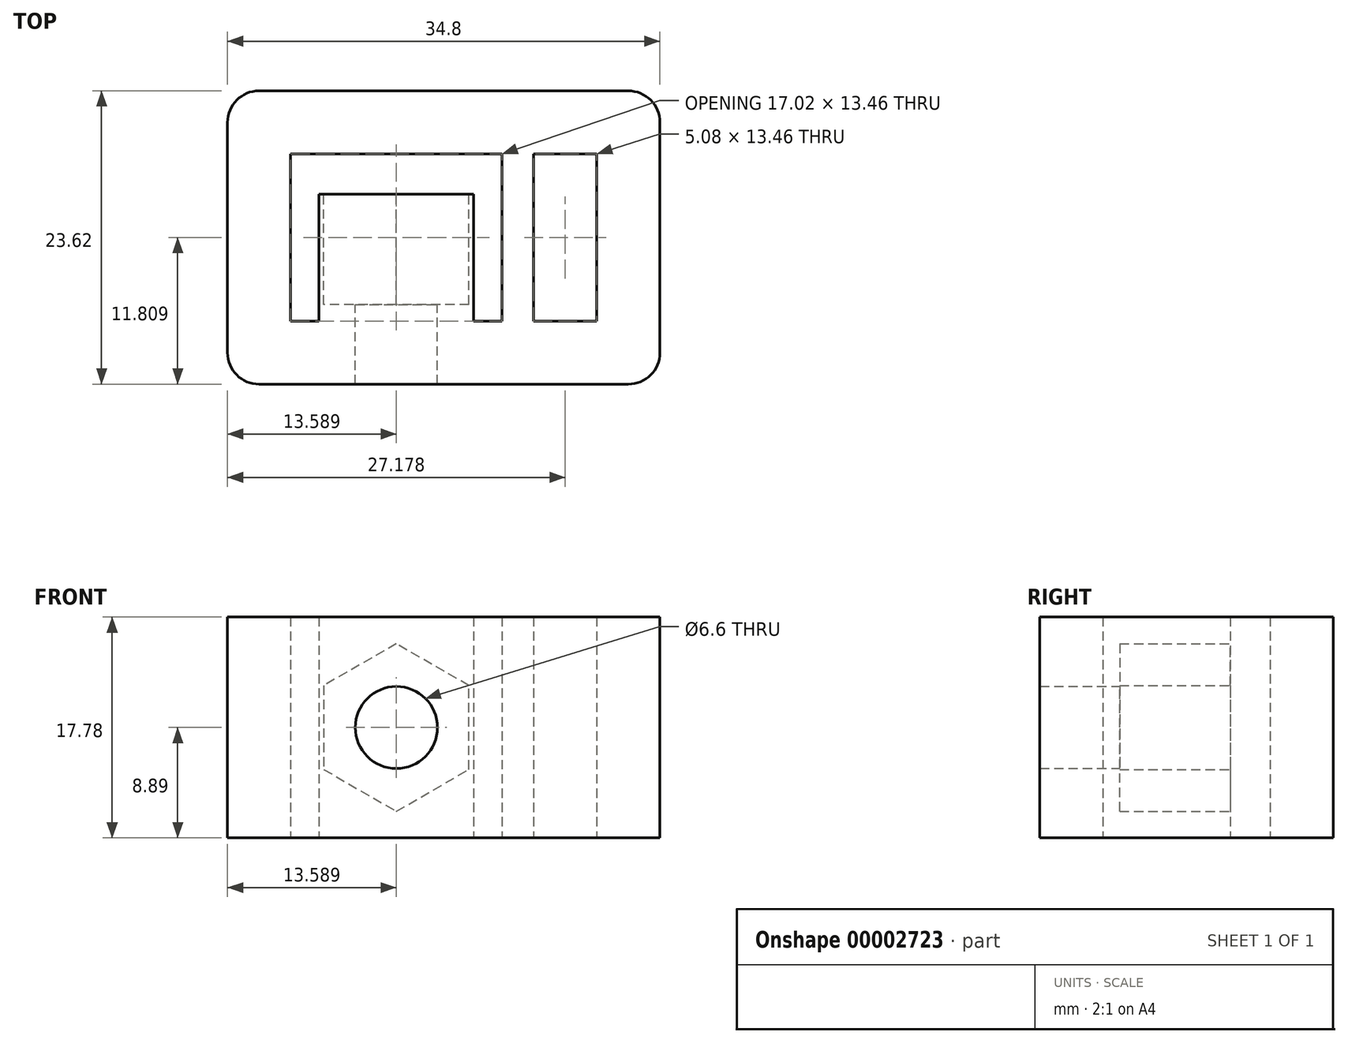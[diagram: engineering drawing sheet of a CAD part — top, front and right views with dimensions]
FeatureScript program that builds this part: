
annotation { "Feature Type Name" : "Feature", "Feature Type Description" : "" }
export const myFeature = defineFeature(function(context is Context, id is Id, definition is map)
    precondition{}
    {
        {
            var Q0;
            Q0=qCreatedBy(makeId("Top.planeOp"),FACE);
            var sketch = newSketch(context, id + "F0", { "sketchPlane" : qUnion([Q0])});
            skLineSegment(sketch, "E0", {"start": v(0, 0) * mm, "end": v(17.02, 0) * mm});
            skLineSegment(sketch, "E1", {"start": v(17.02, 0) * mm, "end": v(17.02, -13.46) * mm});
            skLineSegment(sketch, "E2", {"start": v(17.02, -13.46) * mm, "end": v(14.73, -13.46) * mm});
            skLineSegment(sketch, "E3", {"start": v(14.73, -13.46) * mm, "end": v(14.73, -3.23) * mm});
            skLineSegment(sketch, "E4", {"start": v(14.73, -3.23) * mm, "end": v(2.29, -3.23) * mm});
            skLineSegment(sketch, "E5", {"start": v(2.29, -3.23) * mm, "end": v(2.29, -13.46) * mm});
            skLineSegment(sketch, "E6", {"start": v(2.29, -13.46) * mm, "end": v(0, -13.46) * mm});
            skLineSegment(sketch, "E7", {"start": v(0, -13.46) * mm, "end": v(0, 0) * mm});
            skLineSegment(sketch, "E8", {"start": v(17.02, -13.46) * mm, "end": v(19.56, -13.46) * mm, "construction": true});
            skLineSegment(sketch, "E9", {"start": v(17.02, 0) * mm, "end": v(19.56, 0) * mm, "construction": true});
            skLineSegment(sketch, "E10", {"start": v(19.56, -13.46) * mm, "end": v(19.56, 0) * mm});
            skLineSegment(sketch, "E11", {"start": v(24.64, 0) * mm, "end": v(24.64, -13.46) * mm});
            skLineSegment(sketch, "E12", {"start": v(24.64, -13.46) * mm, "end": v(19.56, -13.46) * mm});
            skLineSegment(sketch, "E13", {"start": v(24.64, 0) * mm, "end": v(19.56, 0) * mm});
            skSolve(sketch);
        }
        {
            var Q0;
            Q0=qCreatedBy(makeId("Top.planeOp"),FACE);
            var sketch = newSketch(context, id + "F1", { "sketchPlane" : qUnion([Q0])});
            skLineSegment(sketch, "E14", {"start": v(0, 0) * mm, "end": v(0, 5.08) * mm, "construction": true});
            skLineSegment(sketch, "E15", {"start": v(0, 5.08) * mm, "end": v(-5.08, 5.08) * mm, "construction": true});
            skLineSegment(sketch, "E16", {"start": v(24.64, -13.46) * mm, "end": v(24.64, -18.54) * mm, "construction": true});
            skLineSegment(sketch, "E17", {"start": v(24.64, -18.54) * mm, "end": v(29.72, -18.54) * mm, "construction": true});
            skSolve(sketch);
        }
        {
            var Q0;
            Q0=qCreatedBy(makeId("Top.planeOp"),FACE);
            var sketch = newSketch(context, id + "F2", { "sketchPlane" : qUnion([Q0])});
            skLineSegment(sketch, "E18.bottom", {"start": v(-5.08, 5.08) * mm, "end": v(29.72, 5.08) * mm});
            skLineSegment(sketch, "E18.top", {"start": v(-5.08, -18.54) * mm, "end": v(29.72, -18.54) * mm});
            skLineSegment(sketch, "E18.left", {"start": v(-5.08, 5.08) * mm, "end": v(-5.08, -18.54) * mm});
            skLineSegment(sketch, "E18.right", {"start": v(29.72, 5.08) * mm, "end": v(29.72, -18.54) * mm});
            skSolve(sketch);
        }
        {
            var Q0;
            Q0=makeQuery(id+"F2.imprint","IMPRINT",FACE,{"disambiguationData":[TD([[makeQuery(id+"F2.imprint","IMPRINT",EDGE,{"derivedFrom":sQuery(id+"F2.wireOp",EDGE,"E18.bottom")}),-1.0]])]});
            extrude(context, id + "F3", {"entities" : qUnion([Q0]), "depth" : 17.78 * mm});
        }
        {
            var Q0;
            {Q0=qUnion([makeQuery(id+"F0.imprint","IMPRINT",FACE,{"disambiguationData":[TD([[makeQuery(id+"F0.imprint","IMPRINT",EDGE,{"derivedFrom":sQuery(id+"F0.wireOp",EDGE,"E0")}),-1.0]])]}),makeQuery(id+"F0.imprint","IMPRINT",FACE,{"disambiguationData":[TD([[makeQuery(id+"F0.imprint","IMPRINT",EDGE,{"derivedFrom":sQuery(id+"F0.wireOp",EDGE,"E10")}),-1.0]])]})]);}
            extrude(context, id + "F4", {"entities" : qUnion([Q0]), "operationType" : NewBodyOperationType.REMOVE, "depth" : 17.78 * mm});
        }
        {
            var Q0;
            Q0=makeQuery(id+"F4.boolean.opBoolean","COPY",FACE,{"derivedFrom":makeQuery(id+"F4.opExtrude","SWEPT_FACE",FACE,{"disambiguationData":[OSD([sQuery(id+"F0.wireOp",EDGE,"E4")])]})});
            var sketch = newSketch(context, id + "F5", { "sketchPlane" : qUnion([Q0])});
            skLineSegment(sketch, "E19", {"start": v(-14.73, 17.78) * mm, "end": v(-2.29, 0) * mm, "construction": true});
            skCircle(sketch, "E20.cCircle", {"center": v(-8.5, 8.9) * mm, "radius": 5.84 * mm, "construction": true});
            skLineSegment(sketch, "E20.0", {"start": v(-2.67, 12.26) * mm, "end": v(-2.67, 5.52) * mm});
            skLineSegment(sketch, "E20.1", {"start": v(-2.67, 5.52) * mm, "end": v(-8.5, 2.14) * mm});
            skLineSegment(sketch, "E20.2", {"start": v(-8.5, 2.14) * mm, "end": v(-14.35, 5.52) * mm});
            skLineSegment(sketch, "E20.3", {"start": v(-14.35, 5.52) * mm, "end": v(-14.35, 12.26) * mm});
            skLineSegment(sketch, "E20.4", {"start": v(-14.35, 12.26) * mm, "end": v(-8.5, 15.64) * mm});
            skLineSegment(sketch, "E20.5", {"start": v(-8.5, 15.64) * mm, "end": v(-2.67, 12.26) * mm});
            skPoint(sketch, "E20.0.midPoint", {"position": v(-2.67, 8.9) * mm});
            skSolve(sketch);
        }
        {
            var Q0;
            Q0=makeQuery(id+"F5.imprint","IMPRINT",FACE,{"disambiguationData":[TD([[makeQuery(id+"F5.imprint","IMPRINT",EDGE,{"derivedFrom":sQuery(id+"F5.wireOp",EDGE,"E20.0")}),1.0]])]});
            var sketch = newSketch(context, id + "F6", { "sketchPlane" : qUnion([Q0])});
            skCircle(sketch, "E21", {"center": v(-8.5, 8.9) * mm, "radius": 3.3 * mm});
            skSolve(sketch);
        }
        {
            var Q0;
            Q0=makeQuery(id+"F5.imprint","IMPRINT",FACE,{"disambiguationData":[TD([[makeQuery(id+"F5.imprint","IMPRINT",EDGE,{"derivedFrom":sQuery(id+"F5.wireOp",EDGE,"E20.0")}),-1.0]])]});
            extrude(context, id + "F7", {"entities" : qUnion([Q0]), "operationType" : NewBodyOperationType.REMOVE, "oppositeDirection" : true, "depth" : 8.9 * mm});
        }
        {
            var Q0;
            Q0=makeQuery(id+"F6.imprint","IMPRINT",FACE,{"disambiguationData":[TD([[makeQuery(id+"F6.imprint","IMPRINT",EDGE,{"derivedFrom":sQuery(id+"F6.wireOp",EDGE,"E21")}),1.0]])]});
            extrude(context, id + "F8", {"entities" : qUnion([Q0]), "operationType" : NewBodyOperationType.REMOVE, "oppositeDirection" : true, "depth" : 25.4 * mm});
        }
        {
            var Q0;
            Q0=makeQuery(id+"F6.imprint","IMPRINT",FACE,{"disambiguationData":[TD([[makeQuery(id+"F6.imprint","IMPRINT",EDGE,{"derivedFrom":makeQuery(id+"F5.imprint","IMPRINT",EDGE,{"derivedFrom":sQuery(id+"F5.wireOp",EDGE,"E20.0")})}),1.0]])]});
            var sketch = newSketch(context, id + "F9", { "sketchPlane" : qUnion([Q0])});
            skLineSegment(sketch, "E22.bottom", {"start": v(-2.29, 17.78) * mm, "end": v(-15.08, 17.78) * mm});
            skLineSegment(sketch, "E22.top", {"start": v(-2.29, 5.26) * mm, "end": v(-15.08, 5.26) * mm});
            skLineSegment(sketch, "E22.left", {"start": v(-2.29, 17.78) * mm, "end": v(-2.29, 5.26) * mm});
            skLineSegment(sketch, "E22.right", {"start": v(-15.08, 17.78) * mm, "end": v(-15.08, 5.26) * mm});
            skSolve(sketch);
        }
        {
            var Q0;
            {var subQ7=sQuery(id+"F9.wireOp",EDGE,"E22.right");var subQ14=makeQuery(id+"F6.imprint","IMPRINT",EDGE,{"derivedFrom":makeQuery(id+"F5.imprint","IMPRINT",EDGE,{"derivedFrom":sQuery(id+"F5.wireOp",EDGE,"E20.0")})});var subQ19=makeQuery(id+"F9.imprint","IMPRINT",EDGE,{"derivedFrom":subQ14});var subQ20=sQuery(id+"F9.wireOp",EDGE,"E22.left");Q0=qUnion([makeQuery(id+"F9.imprint","IMPRINT",FACE,{"disambiguationData":[TD([[makeQuery(id+"F9.imprint","IMPRINT",EDGE,{"derivedFrom":subQ7}),1.0]])]}),makeQuery(id+"F9.imprint","IMPRINT",FACE,{"disambiguationData":[TD([[subQ19,-1.0]])]}),makeQuery(id+"F9.imprint","IMPRINT",FACE,{"disambiguationData":[TD([[makeQuery(id+"F9.imprint","IMPRINT",EDGE,{"derivedFrom":subQ20}),-1.0]])]})]);}
            extrude(context, id + "F10", {"entities" : qUnion([Q0]), "operationType" : NewBodyOperationType.REMOVE, "oppositeDirection" : true, "depth" : 3.8 * mm});
        }
        {
            var Q0;
            Q0=makeQuery(id+"F3.opExtrude","SWEPT_EDGE",EDGE,{"disambiguationData":[OSD([sQuery(id+"F2.wireOp",EDGE,"E18.top"),sQuery(id+"F2.wireOp",EDGE,"E18.right")])]});
            var Q1;
            Q1=makeQuery(id+"F3.opExtrude","SWEPT_EDGE",EDGE,{"disambiguationData":[OSD([sQuery(id+"F2.wireOp",EDGE,"E18.top"),sQuery(id+"F2.wireOp",EDGE,"E18.left")])]});
            var Q2;
            Q2=makeQuery(id+"F3.opExtrude","SWEPT_EDGE",EDGE,{"disambiguationData":[OSD([sQuery(id+"F2.wireOp",EDGE,"E18.bottom"),sQuery(id+"F2.wireOp",EDGE,"E18.right")])]});
            var Q3;
            Q3=makeQuery(id+"F3.opExtrude","SWEPT_EDGE",EDGE,{"disambiguationData":[OSD([sQuery(id+"F2.wireOp",EDGE,"E18.bottom"),sQuery(id+"F2.wireOp",EDGE,"E18.left")])]});
            fillet(context, id + "F11", {"entities" : qUnion([Q0, Q1, Q2, Q3]), "radius" : 2.54 * mm, "tangentPropagation" : true, "allowEdgeOverflow" : false});
        }
    });
